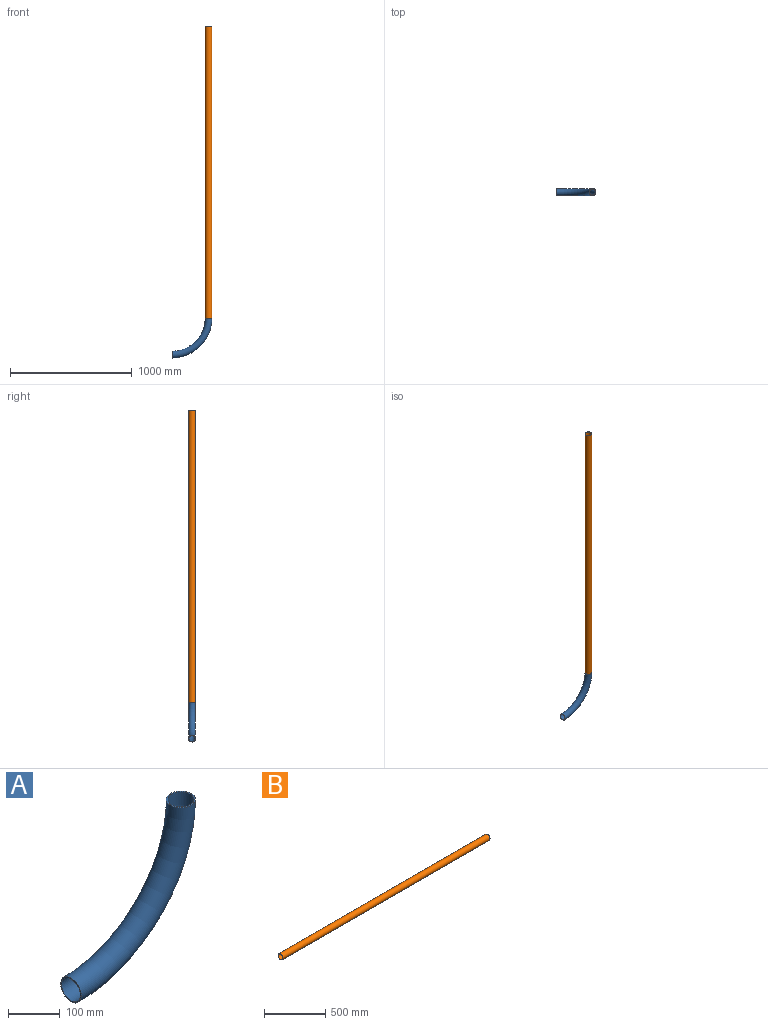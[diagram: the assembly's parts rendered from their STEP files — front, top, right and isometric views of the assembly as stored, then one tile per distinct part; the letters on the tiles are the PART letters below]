
ASSEMBLY  parts=2 mates=1
PART A: 4 faces, bbox 355x56x355 mm
  f0: torus R=300mm, axis (0,-1,0), area 75502.5mm2, adj f1,f2
  f1: plane 56x56mm, normal (-1,0,0), area 420.2mm2, adj f0,f3
  f2: plane 56x56mm, normal (0,0,1), area 420.2mm2, adj f0,f3
  f3: torus R=300mm, axis (0,-1,0), area 82904.7mm2, adj f1,f2
PART B: 4 faces, bbox 2400x56x56 mm
  f0: cylinder r=25.5mm len=2400mm, axis (-1,0,0), area 384530.9mm2, adj f2,f3
  f1: cylinder r=28mm len=2400mm, axis (-1,0,0), area 422230.1mm2, adj f2,f3
  f2: plane 56x56mm, normal (1,0,0), area 420.2mm2, adj f0,f1
  f3: plane 56x56mm, normal (-1,0,0), area 420.2mm2, adj f0,f1
PLACE A t=(-300,0,-625)mm
PLACE B rot(axis=(0.71,0,0.71),180deg) t=(0,0,-325)mm
MATE fastened B.f1 <-> A.f2  axis (0,0,-1) through (0,0,-325)mm
